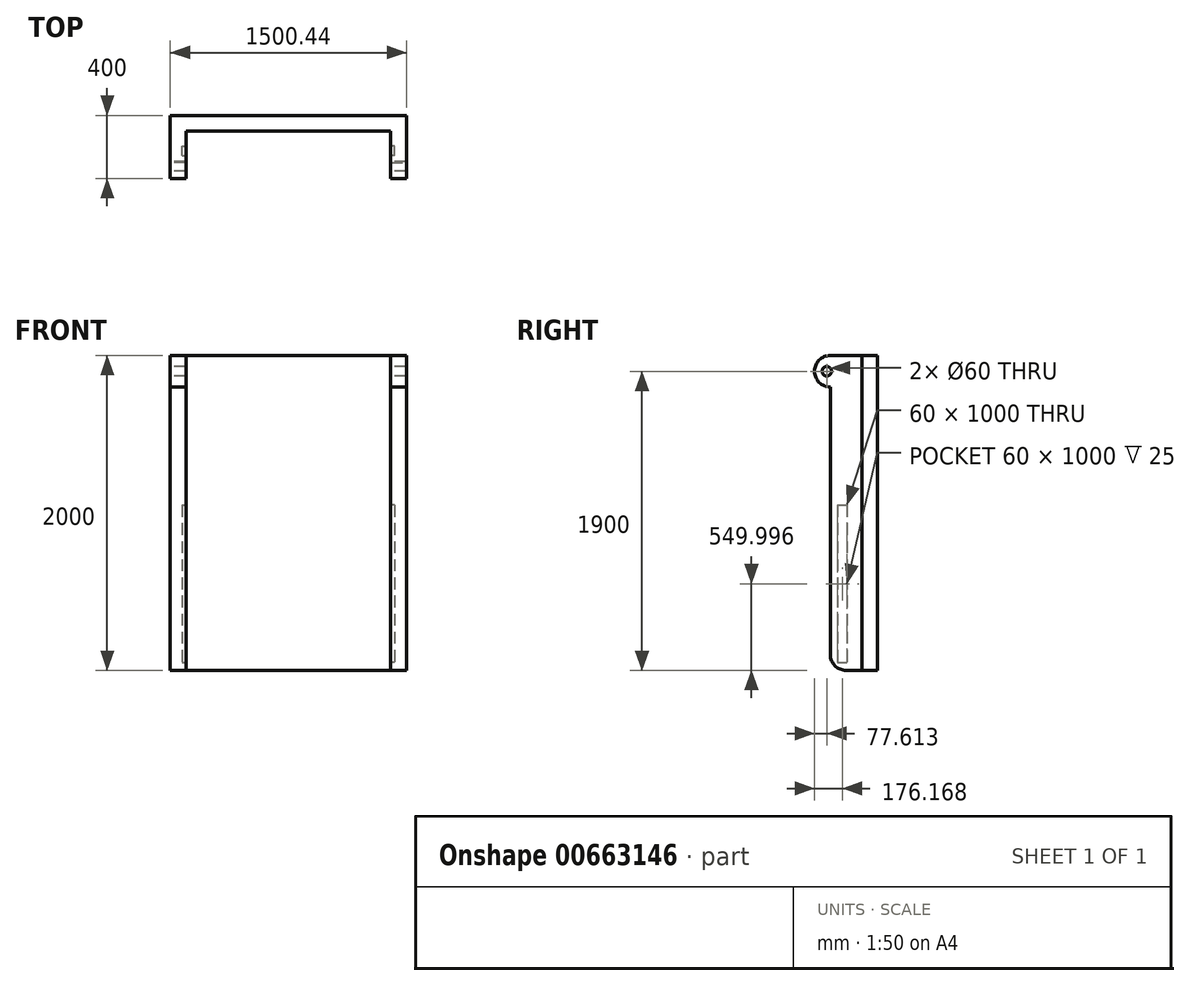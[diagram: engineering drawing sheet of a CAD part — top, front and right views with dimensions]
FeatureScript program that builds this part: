
annotation { "Feature Type Name" : "Feature", "Feature Type Description" : "" }
export const myFeature = defineFeature(function(context is Context, id is Id, definition is map)
    precondition{}
    {
        {
            var Q0;
            Q0=qCreatedBy(makeId("Front.planeOp"),FACE);
            var sketch = newSketch(context, id + "F0", { "sketchPlane" : qUnion([Q0])});
            skLineSegment(sketch, "E0.bottom", {"start": v(-749.78, 1375.38) * mm, "end": v(750.22, 1375.38) * mm});
            skLineSegment(sketch, "E0.top", {"start": v(-749.78, -624.62) * mm, "end": v(750.22, -624.62) * mm});
            skLineSegment(sketch, "E0.left", {"start": v(-749.78, 1375.38) * mm, "end": v(-749.78, -624.62) * mm});
            skLineSegment(sketch, "E0.right", {"start": v(750.22, 1375.38) * mm, "end": v(750.22, -624.62) * mm});
            skSolve(sketch);
        }
        {
            var Q0;
            Q0 = qSketchRegion(id + "F0", true);
            extrude(context, id + "F1", {"entities" : qUnion([Q0]), "depth" : 100 * mm, "offsetDistance" : 25 * mm});
        }
        {
            var Q0;
            Q0=makeQuery(id+"F1.opExtrude","SWEPT_FACE",FACE,{"disambiguationData":[OSD([sQuery(id+"F0.wireOp",EDGE,"E0.left")])]});
            var sketch = newSketch(context, id + "F2", { "sketchPlane" : qUnion([Q0])});
            skLineSegment(sketch, "E1", {"start": v(100, 1375.38) * mm, "end": v(400, 1375.38) * mm});
            skLineSegment(sketch, "E2", {"start": v(400, 1375.38) * mm, "end": v(400, 1175.38) * mm});
            skLineSegment(sketch, "E3", {"start": v(400, 1175.38) * mm, "end": v(300, 1175.38) * mm});
            skLineSegment(sketch, "E4", {"start": v(300, 1175.38) * mm, "end": v(300, -624.62) * mm});
            skLineSegment(sketch, "E5", {"start": v(300, -624.62) * mm, "end": v(100, -624.62) * mm});
            skLineSegment(sketch, "E6", {"start": v(100, -624.62) * mm, "end": v(100, 1375.38) * mm});
            skSolve(sketch);
        }
        {
            var Q0;
            Q0 = qSketchRegion(id + "F2", true);
            extrude(context, id + "F3", {"entities" : qUnion([Q0]), "operationType" : NewBodyOperationType.ADD, "oppositeDirection" : true, "depth" : 100 * mm, "offsetDistance" : 25 * mm});
        }
        {
            var Q0;
            Q0=makeQuery(id+"F3.opExtrude","CAP_FACE",FACE,{"disambiguationData":[OSD([sQuery(id+"F2.wireOp",EDGE,"E1"),sQuery(id+"F2.wireOp",EDGE,"E2"),sQuery(id+"F2.wireOp",EDGE,"E3"),sQuery(id+"F2.wireOp",EDGE,"E4"),sQuery(id+"F2.wireOp",EDGE,"E5"),sQuery(id+"F2.wireOp",EDGE,"E6")])],"isStart":false});
            var sketch = newSketch(context, id + "F4", { "sketchPlane" : qUnion([Q0])});
            skLineSegment(sketch, "E7.bottom", {"start": v(-253.83, 425.38) * mm, "end": v(-193.83, 425.38) * mm});
            skLineSegment(sketch, "E7.top", {"start": v(-253.83, -574.62) * mm, "end": v(-193.83, -574.62) * mm});
            skLineSegment(sketch, "E7.left", {"start": v(-253.83, 425.38) * mm, "end": v(-253.83, -574.62) * mm});
            skLineSegment(sketch, "E7.right", {"start": v(-193.83, 425.38) * mm, "end": v(-193.83, -574.62) * mm});
            skSolve(sketch);
        }
        {
            var Q0;
            Q0 = qSketchRegion(id + "F4", true);
            extrude(context, id + "F5", {"entities" : qUnion([Q0]), "operationType" : NewBodyOperationType.REMOVE, "oppositeDirection" : true, "depth" : 25 * mm, "offsetDistance" : 25 * mm});
        }
        {
            var Q0;
            Q0=makeQuery(id+"F1.opExtrude","SWEPT_BODY",BODY,{"disambiguationData":[OSD([sQuery(id+"F0.wireOp",EDGE,"E0.bottom"),sQuery(id+"F0.wireOp",EDGE,"E0.top"),sQuery(id+"F0.wireOp",EDGE,"E0.left"),sQuery(id+"F0.wireOp",EDGE,"E0.right")])]});
            var Q1;
            Q1=qCreatedBy(makeId("Right.planeOp"),FACE);
            mirror(context, id + "F6", {"operationType" : NewBodyOperationType.ADD, "entities" : qUnion([Q0]), "mirrorPlane" : qUnion([Q1])});
        }
        {
            var Q0;
            Q0=makeQuery(id+"F3.boolean.opBoolean","MERGE",FACE,{"derivedFrom":[makeQuery(id+"F1.opExtrude","SWEPT_FACE",FACE,{"disambiguationData":[OSD([sQuery(id+"F0.wireOp",EDGE,"E0.left")])]}),makeQuery(id+"F3.opExtrude","CAP_FACE",FACE,{"disambiguationData":[OSD([sQuery(id+"F2.wireOp",EDGE,"E1"),sQuery(id+"F2.wireOp",EDGE,"E2"),sQuery(id+"F2.wireOp",EDGE,"E3"),sQuery(id+"F2.wireOp",EDGE,"E4"),sQuery(id+"F2.wireOp",EDGE,"E5"),sQuery(id+"F2.wireOp",EDGE,"E6")])],"isStart":true})]});
            var sketch = newSketch(context, id + "F7", { "sketchPlane" : qUnion([Q0])});
            skCircle(sketch, "E8", {"center": v(322.39, 1275.38) * mm, "radius": 30 * mm});
            skSolve(sketch);
        }
        {
            var Q0;
            Q0 = qSketchRegion(id + "F7", true);
            extrude(context, id + "F8", {"entities" : qUnion([Q0]), "operationType" : NewBodyOperationType.REMOVE, "endBound" : BoundingType.THROUGH_ALL, "oppositeDirection" : true, "depth" : 25 * mm, "offsetDistance" : 25 * mm});
        }
        {
            var Q0;
            Q0=makeQuery(id+"F3.opExtrude","SWEPT_EDGE",EDGE,{"disambiguationData":[OSD([sQuery(id+"F2.wireOp",EDGE,"E2"),sQuery(id+"F2.wireOp",EDGE,"E3")])]});
            var Q1;
            Q1=makeQuery(id+"F6.opPattern","COPY",EDGE,{"derivedFrom":makeQuery(id+"F3.opExtrude","SWEPT_EDGE",EDGE,{"disambiguationData":[OSD([sQuery(id+"F2.wireOp",EDGE,"E2"),sQuery(id+"F2.wireOp",EDGE,"E3")])]}),"instanceName":"1"});
            var Q2;
            Q2=makeQuery(id+"F3.opExtrude","SWEPT_EDGE",EDGE,{"disambiguationData":[OSD([sQuery(id+"F2.wireOp",EDGE,"E4"),sQuery(id+"F2.wireOp",EDGE,"E5")])]});
            var Q3;
            Q3=makeQuery(id+"F6.opPattern","COPY",EDGE,{"derivedFrom":makeQuery(id+"F3.opExtrude","SWEPT_EDGE",EDGE,{"disambiguationData":[OSD([sQuery(id+"F2.wireOp",EDGE,"E4"),sQuery(id+"F2.wireOp",EDGE,"E5")])]}),"instanceName":"1"});
            var Q4;
            Q4=makeQuery(id+"F6.opPattern","COPY",EDGE,{"derivedFrom":makeQuery(id+"F3.opExtrude","SWEPT_EDGE",EDGE,{"disambiguationData":[OSD([sQuery(id+"F2.wireOp",EDGE,"E1"),sQuery(id+"F2.wireOp",EDGE,"E2")])]}),"instanceName":"1"});
            var Q5;
            Q5=makeQuery(id+"F3.opExtrude","SWEPT_EDGE",EDGE,{"disambiguationData":[OSD([sQuery(id+"F2.wireOp",EDGE,"E1"),sQuery(id+"F2.wireOp",EDGE,"E2")])]});
            fillet(context, id + "F9", {"entities" : qUnion([Q0, Q1, Q2, Q3, Q4, Q5]), "radius" : 100 * mm, "tangentPropagation" : true, "allowEdgeOverflow" : false});
        }
    });
